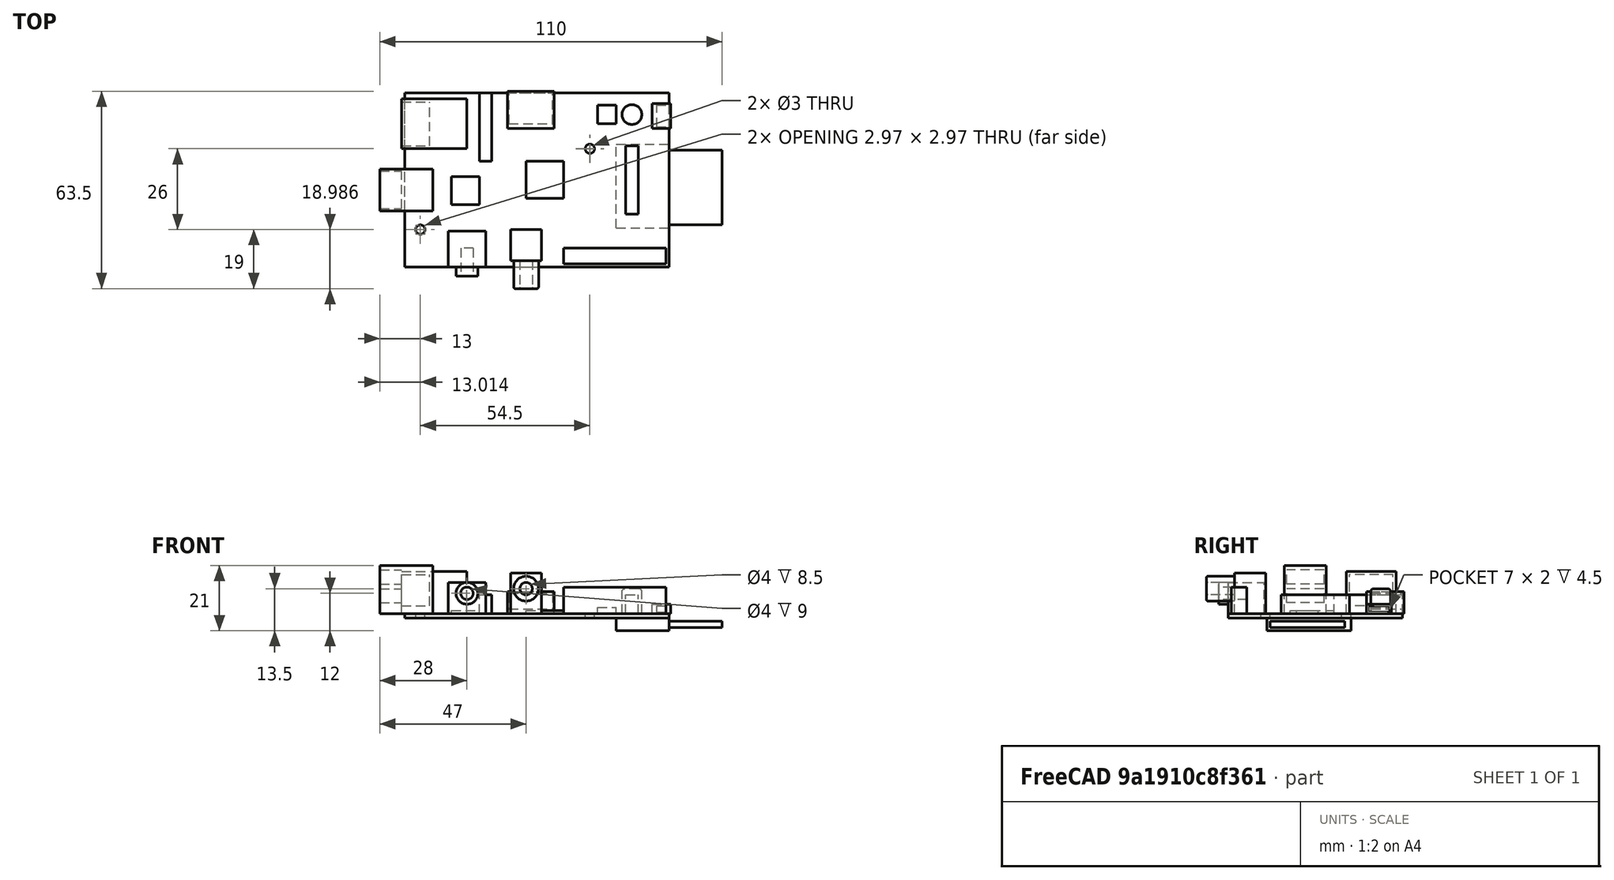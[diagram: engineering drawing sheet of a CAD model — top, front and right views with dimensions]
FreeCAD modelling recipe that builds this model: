
FCSTD DOCUMENT
Label: raspberry pi
objects: Part::Box×20, Part::Cut×9, Part::Cylinder×7, Part::MultiFuse×3, Part::Fillet×2
note: 41 computed .brp shape members not serialized (recipe doc carries the construction recipe); baked Part::Feature solids carry a one-line shape summary decoded from their .brp

FEATURE [Part::Box] Box  label="placa"
  Height = 1.5
  Length = 85
  Width = 56
FEATURE [Part::Box] Box001  label="pines"
  Height = 8.5
  Length = 33
  Placement = pos=(51,1,1.5) rot=(0,0,1;0rad)
  Width = 5
FEATURE [Part::Box] Box002  label="video1"
  Height = 13
  Length = 10
  Placement = pos=(34,2,1.5) rot=(0,0,1;0rad)
  Width = 10
FEATURE [Part::Box] Box003  label="audiocaja"
  Height = 10
  Length = 12
  Placement = pos=(14,0,1.5) rot=(0,0,1;0rad)
  Width = 11.5
FEATURE [Part::Cylinder] Cylinder
  Angle = 360
  Height = 14
  Placement = pos=(20,11,8) rot=(1,0,0;1.5708rad)
  Radius = 3.5
FEATURE [Part::Cylinder] Cylinder001
  Angle = 360
  Height = 10
  Placement = pos=(20,6,8) rot=(1,0,0;1.5708rad)
  Radius = 2
FEATURE [Part::MultiFuse] Fusion
  Shapes = -> [Cylinder,Box003]
FEATURE [Part::Cut] Cut  label="audio"
  Base = -> Fusion
  Tool = -> Cylinder001
FEATURE [Part::Cylinder] Cylinder002
  Angle = 360
  Height = 12
  Placement = pos=(0,0,-1) rot=(0,0,1;0rad)
  Radius = 2
FEATURE [Part::Cylinder] Cylinder003
  Angle = 360
  Height = 10
  Radius = 4
FEATURE [Part::Cut] Cut001
  Base = -> Cylinder003
  Tool = -> Cylinder002
FEATURE [Part::Fillet] Fillet  label="video2"
  Base = -> Cut001
  Edges = 3 edges r=0.5: [Edge1,Edge4,Edge5]
  Placement = pos=(39,3,9.5) rot=(1,0,0;1.5708rad)
FEATURE [Part::MultiFuse] Fusion001  label="video"
  Shapes = -> [Box002,Fillet]
FEATURE [Part::Box] Box004
  Height = 15.5
  Length = 17
  Placement = pos=(-8,18,1.5) rot=(0,0,1;0rad)
  Width = 13.5
FEATURE [Part::Box] Box005
  Height = 4.5
  Length = 8
  Placement = pos=(-9,18.8,5) rot=(0,0,1;0rad)
  Width = 12
FEATURE [Part::Box] Box006
  Height = 4.5
  Length = 8
  Placement = pos=(-9,18.8,11) rot=(0,0,1;0rad)
  Width = 12
FEATURE [Part::Cut] Cut002
  Base = -> Box004
  Tool = -> Box005
FEATURE [Part::Cut] Cut003  label="usb"
  Base = -> Cut002
  Tool = -> Box006
FEATURE [Part::Box] Box007
  Height = 13.5
  Length = 21
  Placement = pos=(-1,38,1.5) rot=(0,0,1;0rad)
  Width = 16
FEATURE [Part::Box] Box008
  Height = 10
  Length = 10
  Placement = pos=(-2,39,4) rot=(0,0,1;0rad)
  Width = 14
FEATURE [Part::Cut] Cut004  label="rj47"
  Base = -> Box007
  Tool = -> Box008
FEATURE [Part::Box] Box009  label="chip001"
  Height = 1
  Length = 9
  Placement = pos=(15,20,1.5) rot=(0,0,1;0rad)
  Width = 9
FEATURE [Part::Box] Box010  label="chip002"
  Height = 1
  Length = 12
  Placement = pos=(39,22,1.5) rot=(0,0,1;0rad)
  Width = 12
FEATURE [Part::Box] Box011  label="conector01"
  Height = 6
  Length = 4
  Placement = pos=(24,34,1.5) rot=(0,0,1;0rad)
  Width = 22
FEATURE [Part::Box] Box012  label="conector02"
  Height = 6
  Length = 4
  Placement = pos=(71,17,1.5) rot=(0,0,1;0rad)
  Width = 22
FEATURE [Part::Cylinder] Cylinder004  label="condensador01"
  Angle = 360
  Height = 8
  Placement = pos=(73,49,1.5) rot=(0,0,1;0rad)
  Radius = 3.2
FEATURE [Part::Fillet] Fillet001  label="condensador"
  Base = -> Cylinder004
  Edges = 1 edges r=1: [Edge1]
FEATURE [Part::Box] Box013  label="chip03"
  Height = 2
  Length = 6
  Placement = pos=(62,46,1.5) rot=(0,0,1;0rad)
  Width = 6
FEATURE [Part::Box] Box014
  Height = 3
  Length = 6
  Placement = pos=(0,0,1.5) rot=(0,0,1;0rad)
  Width = 8
FEATURE [Part::Box] Box015
  Height = 2
  Length = 5
  Placement = pos=(1.5,0.5,2) rot=(0,0,1;0rad)
  Width = 7
FEATURE [Part::Cut] Cut005  label="alimentacion"
  Base = -> Box014
  Placement = pos=(79.5,44.5,0) rot=(0,0,1;0rad)
  Tool = -> Box015
FEATURE [Part::Box] Box016
  Height = 7
  Length = 15
  Placement = pos=(33,44.5,1.5) rot=(0,0,1;0rad)
  Width = 12
FEATURE [Part::Box] Box017
  Height = 5
  Length = 14
  Placement = pos=(33.5,46,3) rot=(0,0,1;0rad)
  Width = 11
FEATURE [Part::Cut] Cut006  label="hdmi"
  Base = -> Box016
  Tool = -> Box017
FEATURE [Part::Box] Box018
  Height = 4
  Length = 17
  Placement = pos=(68,12.5,-4) rot=(0,0,1;0rad)
  Width = 27
FEATURE [Part::Box] Box019
  Height = 2
  Length = 32
  Placement = pos=(70,13.5,-3) rot=(0,0,1;0rad)
  Width = 24
FEATURE [Part::MultiFuse] Fusion002  label="SD"
  Shapes = -> [Box019,Box018]
FEATURE [Part::Cylinder] Cylinder005  label="taladro1"
  Angle = 360
  Height = 3
  Placement = pos=(5,12,-1) rot=(0,0,1;0rad)
  Radius = 1.5
FEATURE [Part::Cylinder] Cylinder006  label="taladro2"
  Angle = 360
  Height = 3
  Placement = pos=(59.5,38,-1) rot=(0,0,1;0rad)
  Radius = 1.5
FEATURE [Part::Cut] Cut007
  Base = -> Box
  Tool = -> Cylinder006
FEATURE [Part::Cut] Cut008  label="placabase"
  Base = -> Cut007
  Tool = -> Cylinder005
